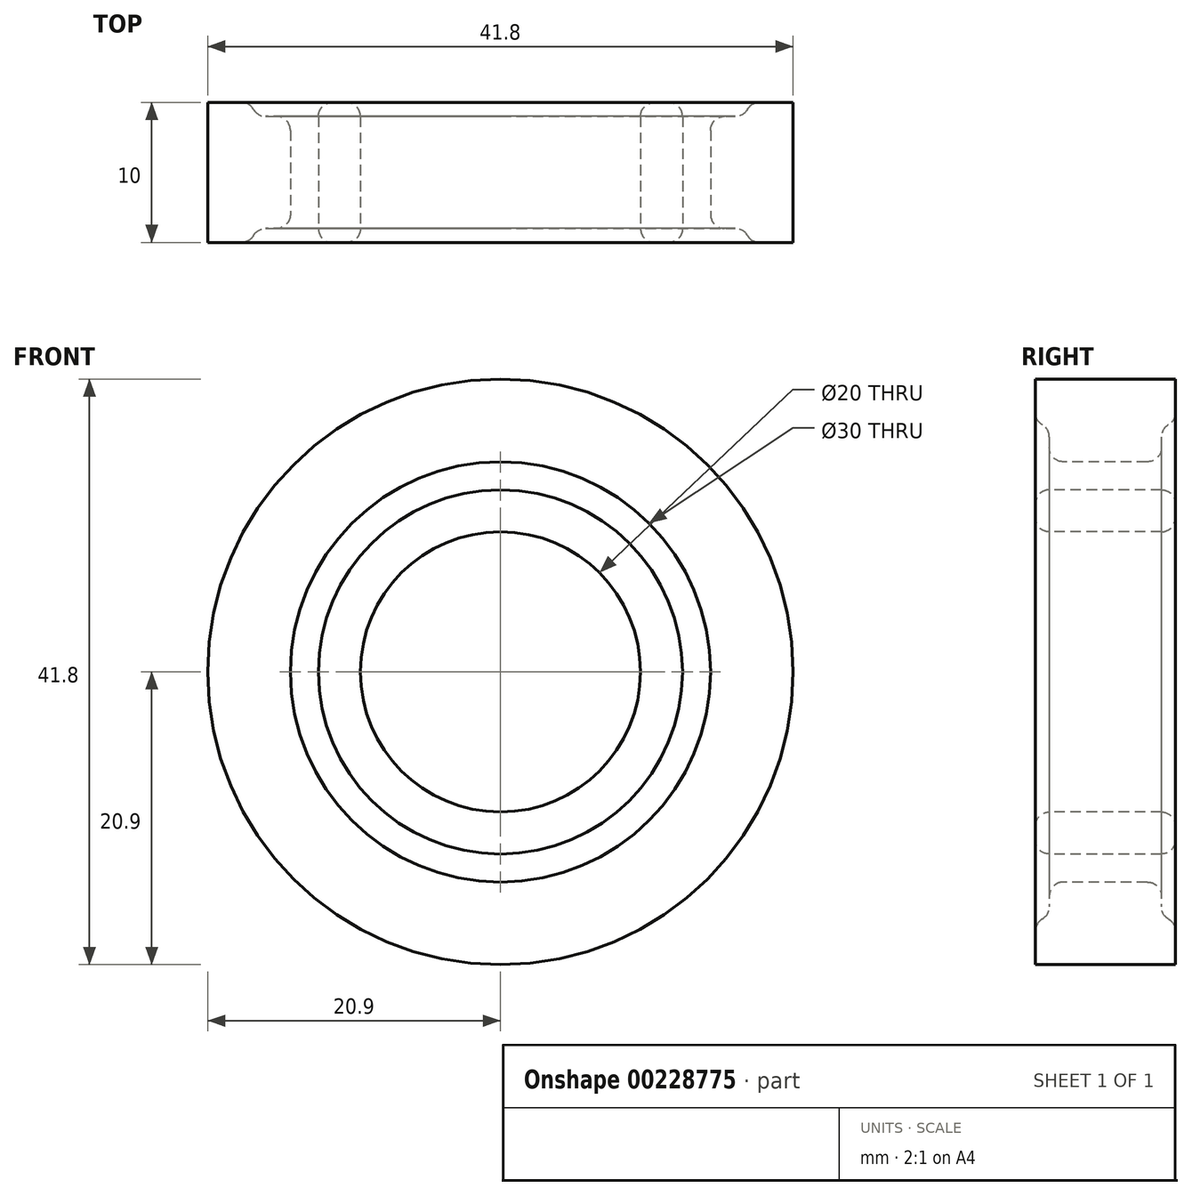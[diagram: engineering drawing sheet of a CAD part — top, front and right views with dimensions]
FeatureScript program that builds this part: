
annotation { "Feature Type Name" : "Feature", "Feature Type Description" : "" }
export const myFeature = defineFeature(function(context is Context, id is Id, definition is map)
    precondition{}
    {
        {
            var Q0;
            Q0=qCreatedBy(makeId("Right.planeOp"),FACE);
            var sketch = newSketch(context, id + "F0", { "sketchPlane" : qUnion([Q0])});
            skLineSegment(sketch, "E0.bottom", {"start": v(-5, 20.9) * mm, "end": v(5, 20.9) * mm});
            skLineSegment(sketch, "E0.left", {"start": v(-5, 20.9) * mm, "end": v(-5, 17.5) * mm});
            skLineSegment(sketch, "E0.right", {"start": v(5, 20.9) * mm, "end": v(5, 17.5) * mm});
            skPoint(sketch, "E0.middle", {"position": v(0, 17.95) * mm});
            skLineSegment(sketch, "E1", {"start": v(-4, 16) * mm, "end": v(-4, 16.5) * mm});
            skPoint(sketch, "E2.visualSharp", {"position": v(4, 17.5) * mm});
            skPoint(sketch, "E3.visualSharp", {"position": v(-4, 15) * mm});
            skPoint(sketch, "E4.visualSharp", {"position": v(4, 15) * mm});
            skLineSegment(sketch, "E5", {"start": v(0, 0) * mm, "end": v(10.37, 0) * mm});
            skLineSegment(sketch, "E6", {"start": v(-5, 17.5) * mm, "end": v(-4, 17.5) * mm});
            skLineSegment(sketch, "E7", {"start": v(-4, 17.5) * mm, "end": v(-4, 15) * mm});
            skLineSegment(sketch, "E8", {"start": v(5, 17.5) * mm, "end": v(4, 17.5) * mm});
            skLineSegment(sketch, "E9", {"start": v(4, 17.5) * mm, "end": v(4, 15) * mm});
            skLineSegment(sketch, "E10", {"start": v(-4, 15) * mm, "end": v(4, 15) * mm});
            skLineSegment(sketch, "E11.bottom", {"start": v(-4, 13) * mm, "end": v(4, 13) * mm});
            skLineSegment(sketch, "E11.top", {"start": v(-4, 10) * mm, "end": v(4, 10) * mm});
            skLineSegment(sketch, "E11.left", {"start": v(-5, 12) * mm, "end": v(-5, 11) * mm});
            skLineSegment(sketch, "E11.right", {"start": v(5, 12) * mm, "end": v(5, 11) * mm});
            skPoint(sketch, "E11.middle", {"position": v(0, 11.5) * mm});
            skPoint(sketch, "E12.visualSharp", {"position": v(-5, 13) * mm});
            skArc(sketch, "E12.filletArc", {"start": v(-4, 13) * mm, "mid": v(-4.7, 12.7) * mm, "end": v(-5, 12) * mm});
            skPoint(sketch, "E13.visualSharp", {"position": v(-5, 10) * mm});
            skArc(sketch, "E13.filletArc", {"start": v(-5, 11) * mm, "mid": v(-4.7, 10.3) * mm, "end": v(-4, 10) * mm});
            skPoint(sketch, "E14.visualSharp", {"position": v(5, 13) * mm});
            skArc(sketch, "E14.filletArc", {"start": v(5, 12) * mm, "mid": v(4.7, 12.7) * mm, "end": v(4, 13) * mm});
            skPoint(sketch, "E15.visualSharp", {"position": v(5, 10) * mm});
            skArc(sketch, "E15.filletArc", {"start": v(4, 10) * mm, "mid": v(4.7, 10.3) * mm, "end": v(5, 11) * mm});
            skSolve(sketch);
        }
        {
            var Q0;
            Q0=makeQuery(id+"F0.imprint","IMPRINT",FACE,{"disambiguationData":[TD([[makeQuery(id+"F0.imprint","IMPRINT",EDGE,{"derivedFrom":sQuery(id+"F0.wireOp",EDGE,"E0.bottom")}),-1.0]])]});
            var Q1;
            Q1=sQuery(id+"F0.wireOp",EDGE,"E5");
            revolve(context, id + "F1", {"entities" : qUnion([Q0]), "axis" : qUnion([Q1]), "revolveType" : RevolveType.FULL});
        }
        {
            var Q0;
            Q0=makeQuery(id+"F1.opRevolve","SWEPT_EDGE",EDGE,{"disambiguationData":[OSD([sQuery(id+"F0.wireOp",EDGE,"E0.right"),sQuery(id+"F0.wireOp",EDGE,"E8")])]});
            var Q1;
            Q1=makeQuery(id+"F1.opRevolve","SWEPT_EDGE",EDGE,{"disambiguationData":[OSD([sQuery(id+"F0.wireOp",EDGE,"E9"),sQuery(id+"F0.wireOp",EDGE,"E10")])]});
            var Q2;
            Q2=makeQuery(id+"F1.opRevolve","SWEPT_EDGE",EDGE,{"disambiguationData":[OSD([sQuery(id+"F0.wireOp",EDGE,"E0.left"),sQuery(id+"F0.wireOp",EDGE,"E6")])]});
            var Q3;
            Q3=makeQuery(id+"F1.opRevolve","SWEPT_EDGE",EDGE,{"disambiguationData":[OSD([sQuery(id+"F0.wireOp",EDGE,"E7"),sQuery(id+"F0.wireOp",EDGE,"E10")])]});
            fillet(context, id + "F2", {"entities" : qUnion([Q0, Q1, Q2, Q3]), "radius" : 1 * mm, "tangentPropagation" : true, "allowEdgeOverflow" : false});
        }
        {
            var Q0;
            Q0=makeQuery(id+"F2.opFillet","BLEND_EDGE",EDGE,{"blendedFrom":[makeQuery(id+"F1.opRevolve","SWEPT_EDGE",EDGE,{"disambiguationData":[OSD([sQuery(id+"F0.wireOp",EDGE,"E0.left"),sQuery(id+"F0.wireOp",EDGE,"E6")])]}),makeQuery(id+"F1.opRevolve","SWEPT_FACE",FACE,{"disambiguationData":[OSD([sQuery(id+"F0.wireOp",EDGE,"E7")])]})],"blendedInto":[makeQuery(id+"F1.opRevolve","SWEPT_FACE",FACE,{"disambiguationData":[OSD([sQuery(id+"F0.wireOp",EDGE,"E7")])]})]});
            var Q1;
            Q1=makeQuery(id+"F2.opFillet","BLEND_EDGE",EDGE,{"blendedFrom":[makeQuery(id+"F1.opRevolve","SWEPT_EDGE",EDGE,{"disambiguationData":[OSD([sQuery(id+"F0.wireOp",EDGE,"E0.right"),sQuery(id+"F0.wireOp",EDGE,"E8")])]}),makeQuery(id+"F1.opRevolve","SWEPT_FACE",FACE,{"disambiguationData":[OSD([sQuery(id+"F0.wireOp",EDGE,"E9")])]})],"blendedInto":[makeQuery(id+"F1.opRevolve","SWEPT_FACE",FACE,{"disambiguationData":[OSD([sQuery(id+"F0.wireOp",EDGE,"E9")])]})]});
            fillet(context, id + "F3", {"entities" : qUnion([Q0, Q1]), "radius" : 1 * mm, "tangentPropagation" : true, "allowEdgeOverflow" : false});
        }
        {
            var Q0;
            Q0=makeQuery(id+"F0.imprint","IMPRINT",FACE,{"disambiguationData":[TD([[makeQuery(id+"F0.imprint","IMPRINT",EDGE,{"derivedFrom":sQuery(id+"F0.wireOp",EDGE,"E11.bottom")}),-1.0]])]});
            var Q1;
            Q1=sQuery(id+"F0.wireOp",EDGE,"E5");
            revolve(context, id + "F4", {"entities" : qUnion([Q0]), "axis" : qUnion([Q1]), "revolveType" : RevolveType.FULL});
        }
    });
